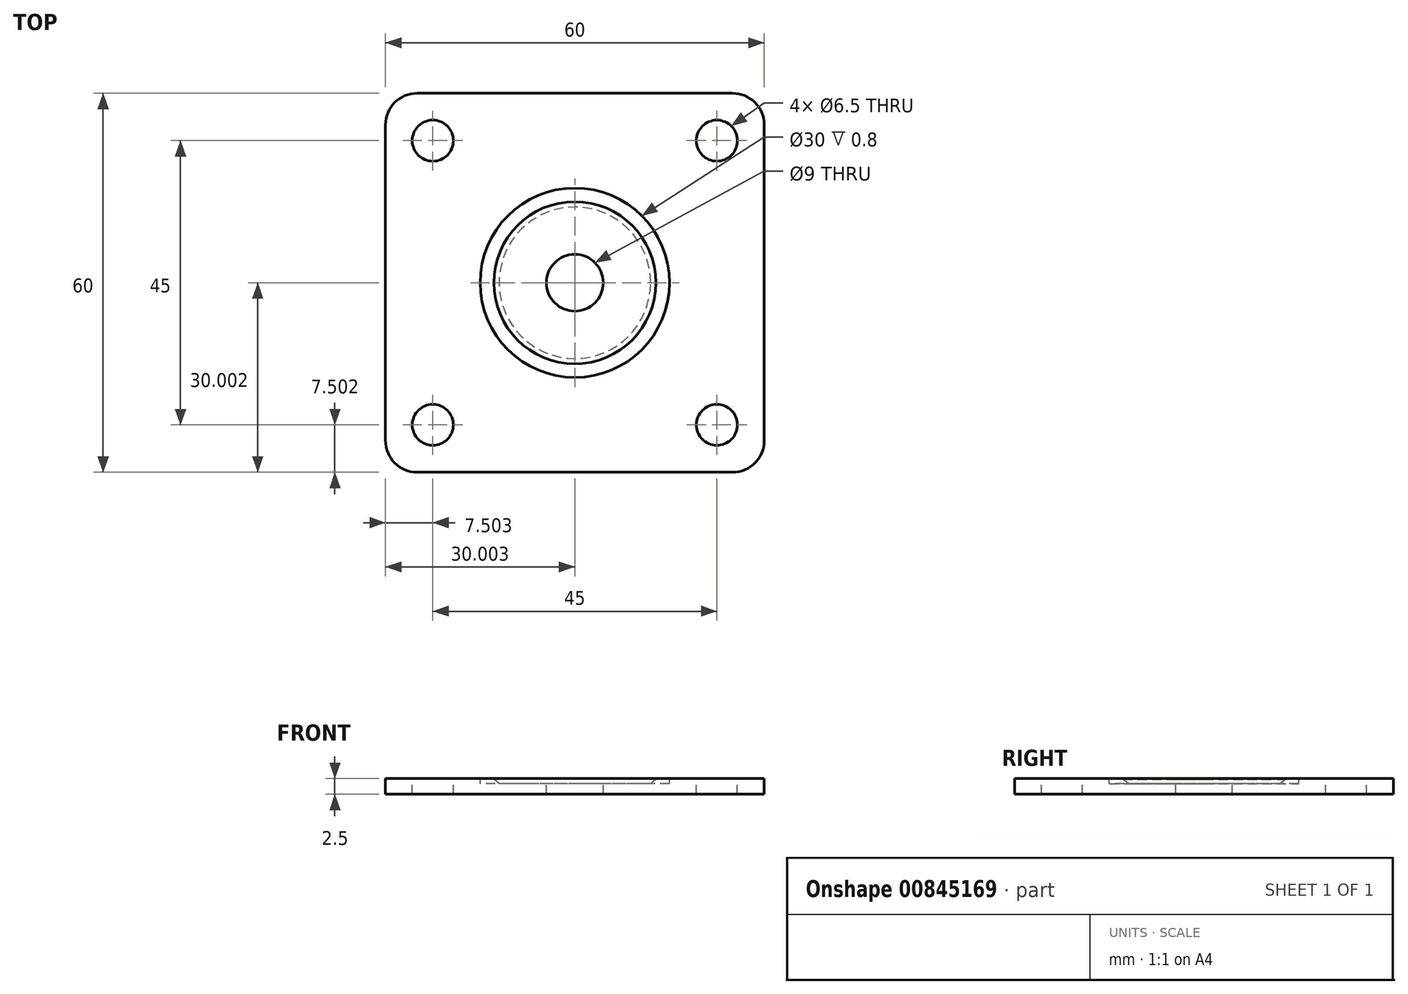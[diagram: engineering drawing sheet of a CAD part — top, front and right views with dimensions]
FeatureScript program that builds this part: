
annotation { "Feature Type Name" : "Feature", "Feature Type Description" : "" }
export const myFeature = defineFeature(function(context is Context, id is Id, definition is map)
    precondition{}
    {
        {
            var Q0;
            Q0=qCreatedBy(makeId("Top.planeOp"),FACE);
            var sketch = newSketch(context, id + "F0", { "sketchPlane" : qUnion([Q0])});
            skLineSegment(sketch, "E0.bottom", {"start": v(-7.13, 8.6) * mm, "end": v(52.87, 8.6) * mm});
            skLineSegment(sketch, "E0.top", {"start": v(-7.13, -51.4) * mm, "end": v(52.87, -51.4) * mm});
            skLineSegment(sketch, "E0.left", {"start": v(-7.13, 8.6) * mm, "end": v(-7.13, -51.4) * mm});
            skLineSegment(sketch, "E0.right", {"start": v(52.87, 8.6) * mm, "end": v(52.87, -51.4) * mm});
            skSolve(sketch);
        }
        {
            var Q0;
            Q0 = qSketchRegion(id + "F0", true);
            extrude(context, id + "F1", {"entities" : qUnion([Q0]), "depth" : 2.5 * mm, "offsetDistance" : 25 * mm});
        }
        {
            var Q0;
            Q0=makeQuery(id+"F1.opExtrude","CAP_FACE",FACE,{"disambiguationData":[OSD([sQuery(id+"F0.wireOp",EDGE,"E0.bottom"),sQuery(id+"F0.wireOp",EDGE,"E0.top"),sQuery(id+"F0.wireOp",EDGE,"E0.left"),sQuery(id+"F0.wireOp",EDGE,"E0.right")])],"isStart":false});
            var sketch = newSketch(context, id + "F2", { "sketchPlane" : qUnion([Q0])});
            skLineSegment(sketch, "E1.bottom", {"start": v(45.37, -43.9) * mm, "end": v(0.37, -43.9) * mm, "construction": true});
            skLineSegment(sketch, "E1.top", {"start": v(45.37, 1.1) * mm, "end": v(0.37, 1.1) * mm, "construction": true});
            skLineSegment(sketch, "E1.left", {"start": v(45.37, -43.9) * mm, "end": v(45.37, 1.1) * mm, "construction": true});
            skLineSegment(sketch, "E1.right", {"start": v(0.37, -43.9) * mm, "end": v(0.37, 1.1) * mm, "construction": true});
            skPoint(sketch, "E1.middle", {"position": v(22.87, -21.4) * mm});
            skPoint(sketch, "E1.middle.positionSnap0", {"position": v(22.87, 8.6) * mm});
            skPoint(sketch, "E1.middle.positionSnap1", {"position": v(-7.13, -21.4) * mm});
            skPoint(sketch, "E1.centerSnap0", {"position": v(22.87, 8.6) * mm});
            skPoint(sketch, "E1.centerSnap1", {"position": v(-7.13, -21.4) * mm});
            skCircle(sketch, "E2", {"center": v(0.37, 1.1) * mm, "radius": 3.25 * mm});
            skCircle(sketch, "E3", {"center": v(45.37, 1.1) * mm, "radius": 3.25 * mm});
            skCircle(sketch, "E4", {"center": v(45.37, -43.9) * mm, "radius": 3.25 * mm});
            skCircle(sketch, "E5", {"center": v(0.37, -43.9) * mm, "radius": 3.25 * mm});
            skSolve(sketch);
        }
        {
            var Q0;
            Q0 = qSketchRegion(id + "F2", true);
            extrude(context, id + "F3", {"entities" : qUnion([Q0]), "operationType" : NewBodyOperationType.REMOVE, "oppositeDirection" : true, "depth" : 25 * mm, "offsetDistance" : 25 * mm});
        }
        {
            var Q0;
            Q0=makeQuery(id+"F1.opExtrude","CAP_FACE",FACE,{"disambiguationData":[OSD([sQuery(id+"F0.wireOp",EDGE,"E0.bottom"),sQuery(id+"F0.wireOp",EDGE,"E0.top"),sQuery(id+"F0.wireOp",EDGE,"E0.left"),sQuery(id+"F0.wireOp",EDGE,"E0.right")])],"isStart":false});
            var sketch = newSketch(context, id + "F4", { "sketchPlane" : qUnion([Q0])});
            skCircle(sketch, "E6", {"center": v(22.87, -21.4) * mm, "radius": 15 * mm});
            skPoint(sketch, "E6.centerSnap0", {"position": v(22.87, 8.6) * mm});
            skPoint(sketch, "E6.centerSnap1", {"position": v(-7.13, -21.4) * mm});
            skSolve(sketch);
        }
        {
            var Q0;
            Q0 = qSketchRegion(id + "F4", true);
            extrude(context, id + "F5", {"entities" : qUnion([Q0]), "operationType" : NewBodyOperationType.REMOVE, "oppositeDirection" : true, "depth" : 0.8 * mm, "offsetDistance" : 25 * mm});
        }
        {
            var Q0;
            Q0=makeQuery(id+"F5.boolean.opBoolean","COPY",FACE,{"derivedFrom":makeQuery(id+"F5.opExtrude","CAP_FACE",FACE,{"disambiguationData":[OSD([sQuery(id+"F4.wireOp",EDGE,"E6")])],"isStart":false})});
            var sketch = newSketch(context, id + "F6", { "sketchPlane" : qUnion([Q0])});
            skCircle(sketch, "E7", {"center": v(22.87, -21.4) * mm, "radius": 12 * mm});
            skSolve(sketch);
        }
        {
            var Q0;
            Q0 = qSketchRegion(id + "F6", true);
            extrude(context, id + "F7", {"entities" : qUnion([Q0]), "operationType" : NewBodyOperationType.ADD, "depth" : 0.7 * mm, "offsetDistance" : 25 * mm, "hasDraft" : true, "draftAngle" : 50 * degree});
        }
        {
            var Q0;
            Q0=makeQuery(id+"F7.opExtrude","CAP_FACE",FACE,{"disambiguationData":[OSD([sQuery(id+"F6.wireOp",EDGE,"E7")])],"isStart":false});
            var sketch = newSketch(context, id + "F8", { "sketchPlane" : qUnion([Q0])});
            skCircle(sketch, "E8", {"center": v(22.87, -21.4) * mm, "radius": 4.5 * mm});
            skSolve(sketch);
        }
        {
            var Q0;
            Q0 = qSketchRegion(id + "F8", true);
            extrude(context, id + "F9", {"entities" : qUnion([Q0]), "operationType" : NewBodyOperationType.REMOVE, "oppositeDirection" : true, "depth" : 25 * mm, "offsetDistance" : 25 * mm});
        }
        {
            var Q0;
            Q0=makeQuery(id+"F1.opExtrude","SWEPT_EDGE",EDGE,{"disambiguationData":[OSD([sQuery(id+"F0.wireOp",EDGE,"E0.top"),sQuery(id+"F0.wireOp",EDGE,"E0.left")])]});
            var Q1;
            Q1=makeQuery(id+"F1.opExtrude","SWEPT_EDGE",EDGE,{"disambiguationData":[OSD([sQuery(id+"F0.wireOp",EDGE,"E0.top"),sQuery(id+"F0.wireOp",EDGE,"E0.right")])]});
            var Q2;
            Q2=makeQuery(id+"F1.opExtrude","SWEPT_EDGE",EDGE,{"disambiguationData":[OSD([sQuery(id+"F0.wireOp",EDGE,"E0.bottom"),sQuery(id+"F0.wireOp",EDGE,"E0.right")])]});
            var Q3;
            Q3=makeQuery(id+"F1.opExtrude","SWEPT_EDGE",EDGE,{"disambiguationData":[OSD([sQuery(id+"F0.wireOp",EDGE,"E0.bottom"),sQuery(id+"F0.wireOp",EDGE,"E0.left")])]});
            fillet(context, id + "F10", {"entities" : qUnion([Q0, Q1, Q2, Q3]), "radius" : 5 * mm, "tangentPropagation" : true, "allowEdgeOverflow" : false});
        }
    });
